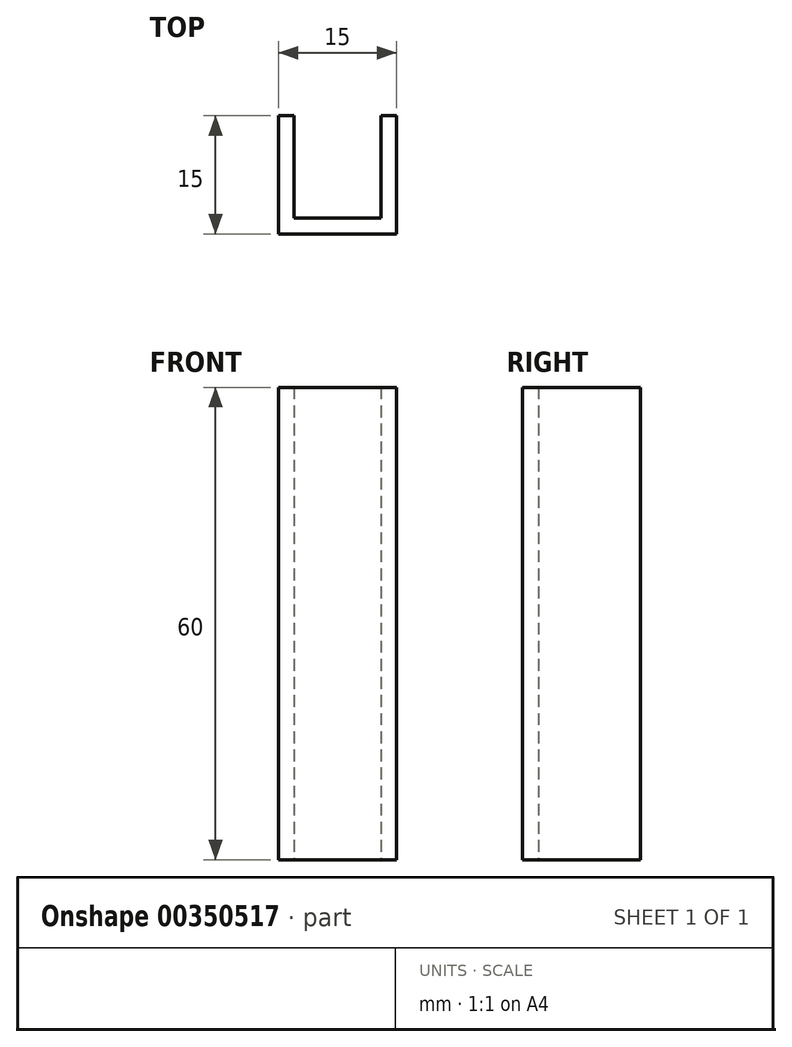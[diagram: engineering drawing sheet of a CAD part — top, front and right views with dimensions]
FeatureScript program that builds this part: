
annotation { "Feature Type Name" : "Feature", "Feature Type Description" : "" }
export const myFeature = defineFeature(function(context is Context, id is Id, definition is map)
    precondition{}
    {
        {
            var Q0;
            Q0=qCreatedBy(makeId("Top.planeOp"),FACE);
            var sketch = newSketch(context, id + "F0", { "sketchPlane" : qUnion([Q0])});
            skLineSegment(sketch, "E0.bottom", {"start": v(-7.5, 7.5) * mm, "end": v(7.5, 7.5) * mm});
            skLineSegment(sketch, "E0.top", {"start": v(-7.5, -7.5) * mm, "end": v(7.5, -7.5) * mm});
            skLineSegment(sketch, "E0.left", {"start": v(-7.5, 7.5) * mm, "end": v(-7.5, -7.5) * mm});
            skLineSegment(sketch, "E0.right", {"start": v(7.5, 7.5) * mm, "end": v(7.5, -7.5) * mm});
            skPoint(sketch, "E0.middle", {"position": v(0, 0) * mm});
            skLineSegment(sketch, "E1.bottom", {"start": v(0, 7.5) * mm, "end": v(-5.5, 7.5) * mm});
            skLineSegment(sketch, "E1.top", {"start": v(0, -5.5) * mm, "end": v(-5.5, -5.5) * mm});
            skLineSegment(sketch, "E1.left", {"start": v(0, 7.5) * mm, "end": v(0, -5.5) * mm});
            skLineSegment(sketch, "E1.right", {"start": v(-5.5, 7.5) * mm, "end": v(-5.5, -5.5) * mm});
            skLineSegment(sketch, "E2.bottom", {"start": v(0, 7.5) * mm, "end": v(5.5, 7.5) * mm});
            skLineSegment(sketch, "E2.top", {"start": v(0, -5.5) * mm, "end": v(5.5, -5.5) * mm});
            skLineSegment(sketch, "E2.right", {"start": v(5.5, 7.5) * mm, "end": v(5.5, -5.5) * mm});
            skSolve(sketch);
        }
        {
            var Q0;
            Q0=makeQuery(id+"F0.imprint","IMPRINT",FACE,{"disambiguationData":[TD([[makeQuery(id+"F0.imprint","IMPRINT",EDGE,{"derivedFrom":sQuery(id+"F0.wireOp",EDGE,"E0.top")}),1.0]])]});
            extrude(context, id + "F1", {"entities" : qUnion([Q0]), "depth" : 60 * mm});
        }
    });
